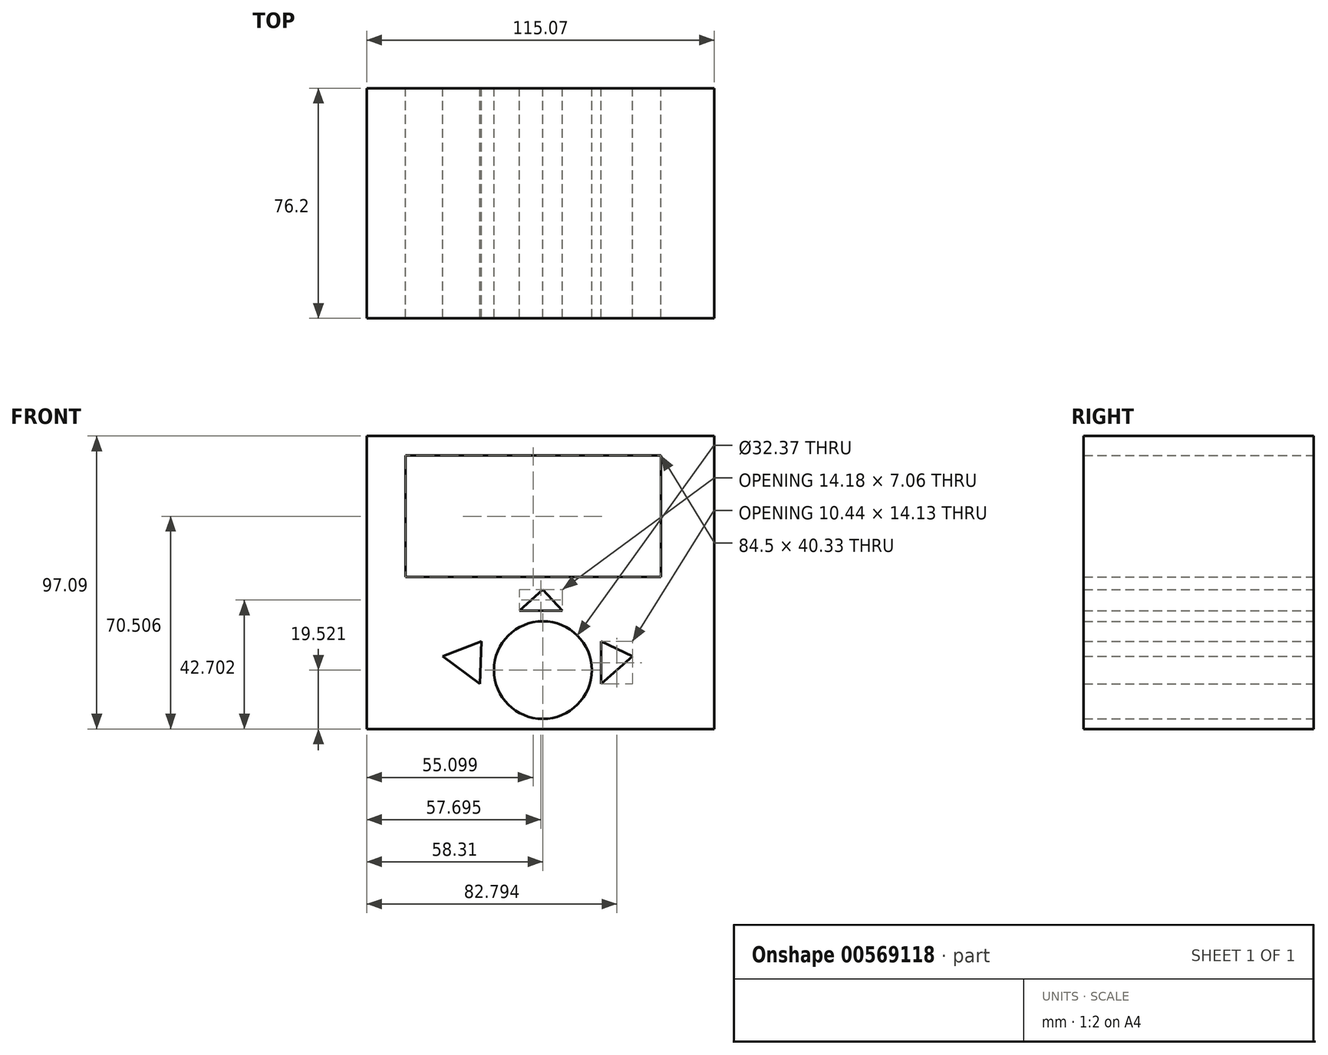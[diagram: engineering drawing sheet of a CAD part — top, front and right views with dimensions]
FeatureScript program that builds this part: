
annotation { "Feature Type Name" : "Feature", "Feature Type Description" : "" }
export const myFeature = defineFeature(function(context is Context, id is Id, definition is map)
    precondition{}
    {
        {
            var Q0;
            Q0=qCreatedBy(makeId("Front.planeOp"),FACE);
            var sketch = newSketch(context, id + "F0", { "sketchPlane" : qUnion([Q0])});
            skLineSegment(sketch, "E0", {"start": v(0, 57.92) * mm, "end": v(-58.3, 57.92) * mm});
            skLineSegment(sketch, "E1", {"start": v(-58.3, 57.92) * mm, "end": v(-58.3, -39.17) * mm});
            skLineSegment(sketch, "E2", {"start": v(-58.3, -39.17) * mm, "end": v(56.76, -39.17) * mm});
            skLineSegment(sketch, "E3", {"start": v(56.76, -39.17) * mm, "end": v(56.76, 57.92) * mm});
            skLineSegment(sketch, "E4", {"start": v(56.76, 57.92) * mm, "end": v(0, 57.92) * mm});
            skLineSegment(sketch, "E5", {"start": v(0, 51.5) * mm, "end": v(-45.46, 51.5) * mm});
            skLineSegment(sketch, "E6", {"start": v(-45.46, 51.5) * mm, "end": v(-45.46, 11.17) * mm});
            skLineSegment(sketch, "E7", {"start": v(-45.46, 11.17) * mm, "end": v(39.04, 11.17) * mm});
            skLineSegment(sketch, "E8", {"start": v(39.04, 11.17) * mm, "end": v(39.04, 51.5) * mm});
            skLineSegment(sketch, "E9", {"start": v(39.04, 51.5) * mm, "end": v(-2.31, 51.5) * mm});
            skLineSegment(sketch, "E10", {"start": v(-2.31, 51.5) * mm, "end": v(0, 51.5) * mm});
            skLineSegment(sketch, "E11", {"start": v(0, 51.5) * mm, "end": v(-2.31, 51.5) * mm});
            skCircle(sketch, "E12", {"center": v(0, -19.65) * mm, "radius": 16.18 * mm});
            skLineSegment(sketch, "E13", {"start": v(-7.7, 0) * mm, "end": v(0, 7.06) * mm});
            skLineSegment(sketch, "E14", {"start": v(0, 7.06) * mm, "end": v(6.47, 0) * mm});
            skLineSegment(sketch, "E15", {"start": v(6.47, 0) * mm, "end": v(-7.7, 0) * mm});
            skLineSegment(sketch, "E16", {"start": v(19.26, -10.15) * mm, "end": v(19.26, -24.27) * mm});
            skLineSegment(sketch, "E17", {"start": v(19.26, -24.27) * mm, "end": v(29.7, -15.1) * mm});
            skLineSegment(sketch, "E18", {"start": v(29.7, -15.1) * mm, "end": v(19.26, -10.15) * mm});
            skLineSegment(sketch, "E19", {"start": v(-20.3, -10.15) * mm, "end": v(-33.12, -15.1) * mm});
            skLineSegment(sketch, "E20", {"start": v(-33.12, -15.1) * mm, "end": v(-20.85, -24.27) * mm});
            skLineSegment(sketch, "E21", {"start": v(-20.85, -24.27) * mm, "end": v(-20.3, -10.15) * mm});
            skSolve(sketch);
        }
        {
            var Q0;
            Q0 = qSketchRegion(id + "F0", true);
            extrude(context, id + "F1", {"entities" : qUnion([Q0]), "depth" : 76.2 * mm, "offsetDistance" : 25.4 * mm});
        }
    });
